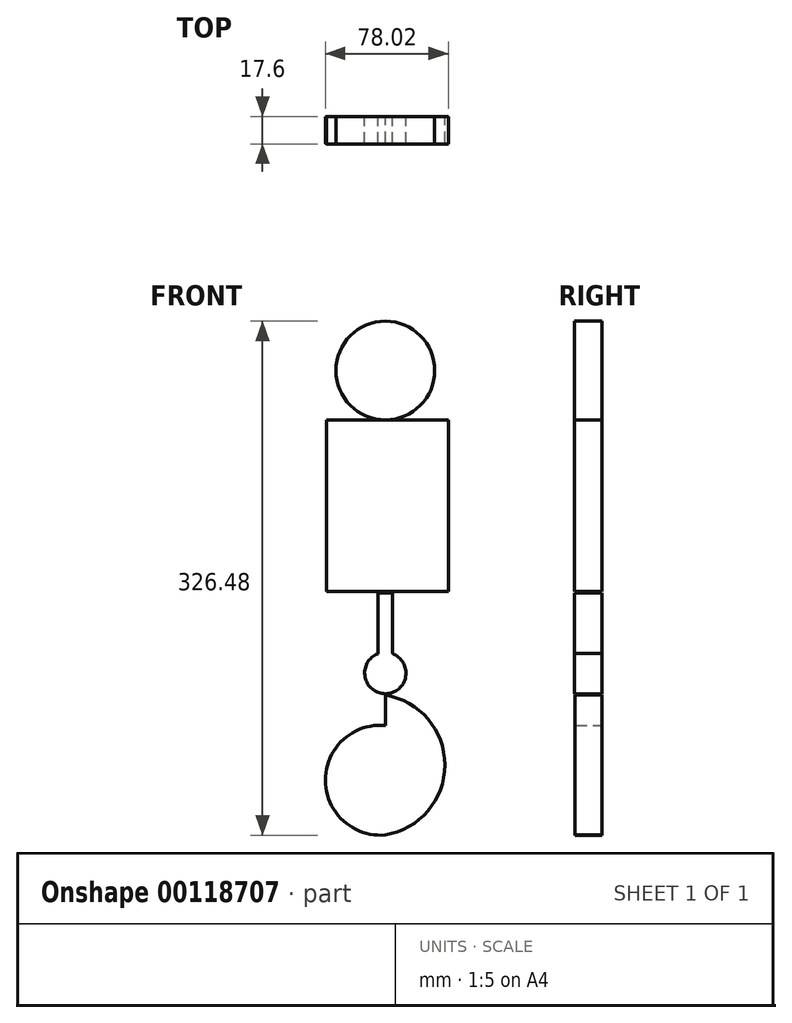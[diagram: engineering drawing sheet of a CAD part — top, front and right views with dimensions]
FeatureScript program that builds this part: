
annotation { "Feature Type Name" : "Feature", "Feature Type Description" : "" }
export const myFeature = defineFeature(function(context is Context, id is Id, definition is map)
    precondition{}
    {
        {
            var Q0;
            Q0=qCreatedBy(makeId("Front.planeOp"),FACE);
            var sketch = newSketch(context, id + "F0", { "sketchPlane" : qUnion([Q0])});
            skArc(sketch, "E0", {"start": v(0, 36.57) * mm, "mid": v(-38.02, 1.78) * mm, "end": v(0, -33.02) * mm});
            skArc(sketch, "E1", {"start": v(0, -33.02) * mm, "mid": v(37.82, 11.43) * mm, "end": v(0, 55.87) * mm});
            skLineSegment(sketch, "E2", {"start": v(0, 55.87) * mm, "end": v(0, 36.57) * mm});
            skSolve(sketch);
        }
        {
            var Q0;
            Q0=makeQuery(id+"F0.imprint","IMPRINT",FACE,{"disambiguationData":[TD([[makeQuery(id+"F0.imprint","IMPRINT",EDGE,{"derivedFrom":sQuery(id+"F0.wireOp",EDGE,"E0")}),1.0]])]});
            extrude(context, id + "F1", {"entities" : qUnion([Q0]), "depth" : 17.15 * mm});
        }
        {
            var Q0;
            Q0=qCreatedBy(makeId("Front.planeOp"),FACE);
            var sketch = newSketch(context, id + "F2", { "sketchPlane" : qUnion([Q0])});
            skCircle(sketch, "E3", {"center": v(0, 69.83) * mm, "radius": 13.12 * mm});
            skLineSegment(sketch, "E4.bottom", {"start": v(4.46, 69.63) * mm, "end": v(-4.77, 69.63) * mm});
            skLineSegment(sketch, "E4.top", {"start": v(4.46, 120.54) * mm, "end": v(-4.77, 120.54) * mm});
            skLineSegment(sketch, "E4.left", {"start": v(4.46, 69.63) * mm, "end": v(4.46, 120.54) * mm});
            skLineSegment(sketch, "E4.right", {"start": v(-4.77, 69.63) * mm, "end": v(-4.77, 120.54) * mm});
            skSolve(sketch);
        }
        {
            var Q0;
            Q0=qCreatedBy(makeId("Front.planeOp"),FACE);
            var sketch = newSketch(context, id + "F3", { "sketchPlane" : qUnion([Q0])});
            skCircle(sketch, "E5", {"center": v(0, 261.96) * mm, "radius": 31.36 * mm});
            skLineSegment(sketch, "E6.bottom", {"start": v(40, 230.53) * mm, "end": v(-37.43, 230.53) * mm});
            skLineSegment(sketch, "E6.top", {"start": v(40, 121.68) * mm, "end": v(-37.43, 121.68) * mm});
            skLineSegment(sketch, "E6.left", {"start": v(40, 230.53) * mm, "end": v(40, 121.68) * mm});
            skLineSegment(sketch, "E6.right", {"start": v(-37.43, 230.53) * mm, "end": v(-37.43, 121.68) * mm});
            skSolve(sketch);
        }
        {
            var Q0;
            {var subQ5=sQuery(id+"F2.wireOp",EDGE,"E4.bottom");Q0=makeQuery(id+"F2.imprint","IMPRINT",FACE,{"disambiguationData":[TD([[makeQuery(id+"F2.imprint","IMPRINT",EDGE,{"derivedFrom":subQ5}),1.0]])]});}
            var Q1;
            {var subQ5=sQuery(id+"F2.wireOp",EDGE,"E4.top");Q1=makeQuery(id+"F2.imprint","IMPRINT",FACE,{"disambiguationData":[TD([[makeQuery(id+"F2.imprint","IMPRINT",EDGE,{"derivedFrom":subQ5}),1.0]])]});}
            var Q2;
            Q2=makeQuery(id+"F3.imprint","IMPRINT",FACE,{"disambiguationData":[TD([[makeQuery(id+"F3.imprint","IMPRINT",EDGE,{"derivedFrom":sQuery(id+"F3.wireOp",EDGE,"E6.bottom")}),1.0]])]});
            var Q3;
            Q3=makeQuery(id+"F3.imprint","IMPRINT",FACE,{"disambiguationData":[TD([[makeQuery(id+"F3.imprint","IMPRINT",EDGE,{"derivedFrom":sQuery(id+"F3.wireOp",EDGE,"E5")}),1.0]])]});
            var Q4;
            {var subQ5=sQuery(id+"F2.wireOp",EDGE,"E4.bottom");Q4=makeQuery(id+"F2.imprint","IMPRINT",FACE,{"disambiguationData":[TD([[makeQuery(id+"F2.imprint","IMPRINT",EDGE,{"derivedFrom":subQ5}),-1.0]])]});}
            extrude(context, id + "F4", {"entities" : qUnion([Q0, Q1, Q2, Q3, Q4]), "depth" : 17.6 * mm});
        }
    });
